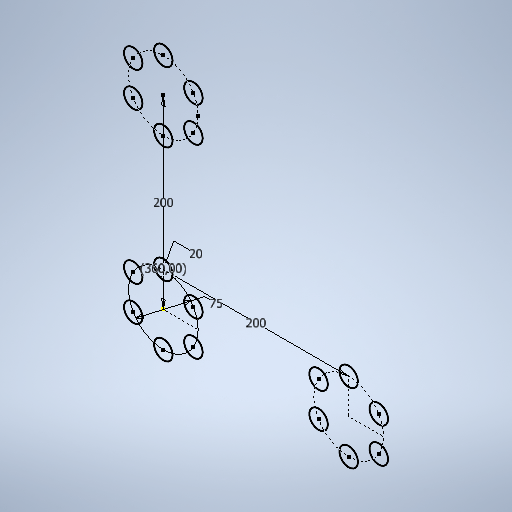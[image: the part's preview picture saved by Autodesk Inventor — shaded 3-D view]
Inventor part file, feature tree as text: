
AUTODESK INVENTOR PART (.ipt)
format: ipt  version: 2025.2 (Build 292293000, 293)  size: 281,600 bytes
history: native  units: mm
features: sketch x7
ambient origin geometry x8: Origin, YZ Plane, XZ Plane, XY Plane, X Axis, Y Axis, Z Axis, Center Point
feature tree (7):
  sketch  "Esboço Suave"  dims[d3=75.0mm]
  sketch  "Esboço Simetria"  dims[d4=60.0mm d6=360.0deg]
  sketch  "Esboço Igual"  dims[d8=20.0mm d10=200.0mm d11=10.0mm d13=10.0mm]
  sketch  "Esboço Circular"  dims[d15=10.0mm d17=10.0mm d18=20.0mm d20=200.0mm]
  sketch  "Esboço - Padrão circular1"  dims[d0=20.0mm]
  sketch  "Esboço - Padrão retangular1"  dims[d1=50.0mm]
  sketch  "Esboço - Padrão retangular2"  dims[d2=20.0mm]
